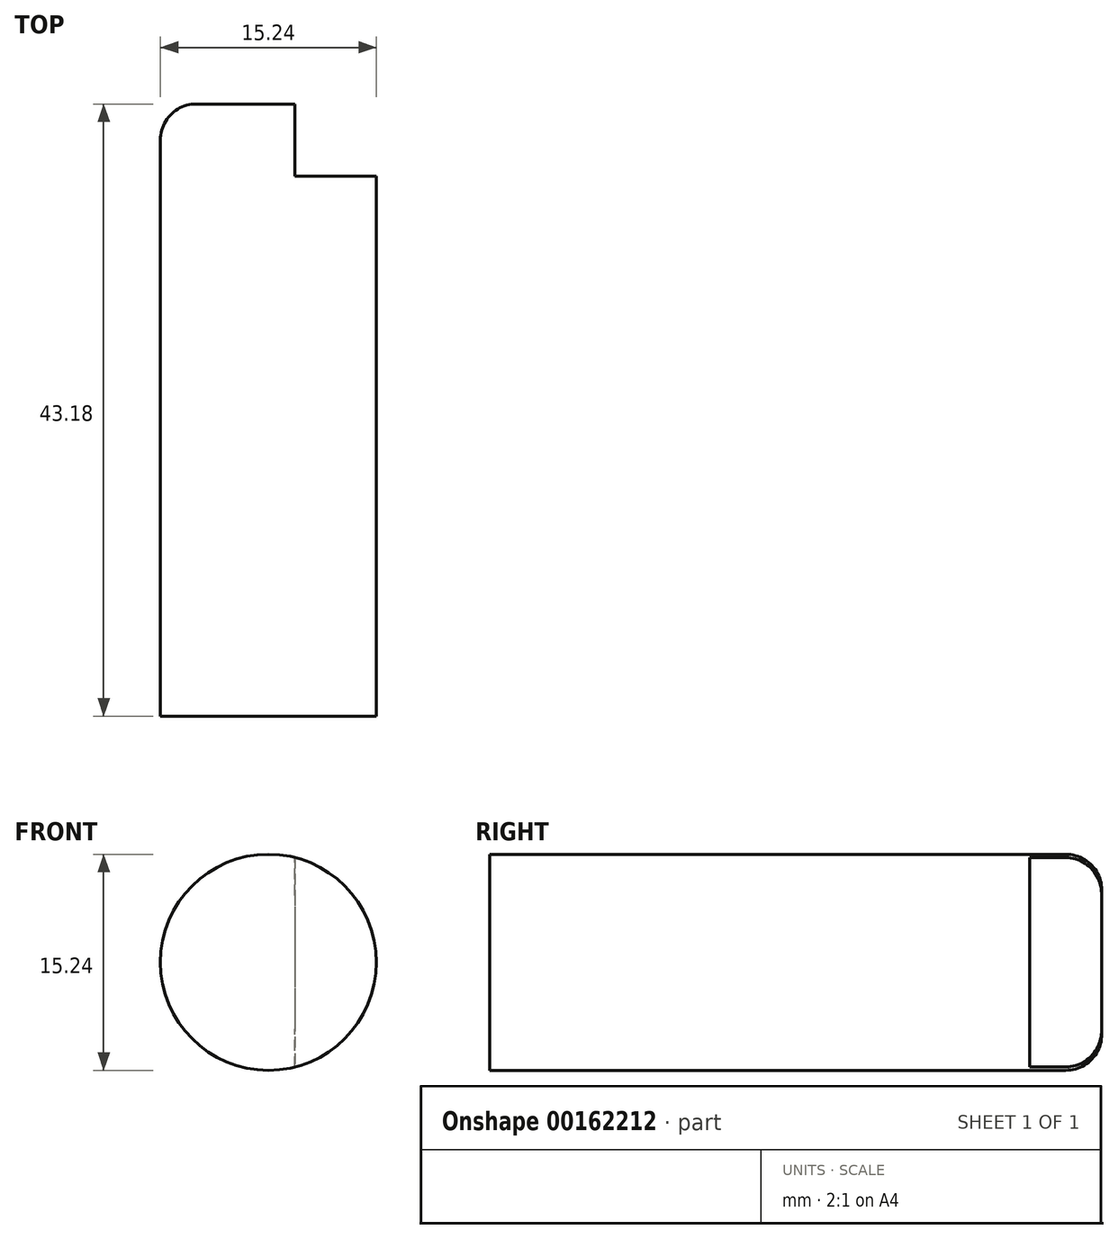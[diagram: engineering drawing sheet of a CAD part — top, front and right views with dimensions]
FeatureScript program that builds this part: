
annotation { "Feature Type Name" : "Feature", "Feature Type Description" : "" }
export const myFeature = defineFeature(function(context is Context, id is Id, definition is map)
    precondition{}
    {
        {
            var Q0;
            Q0=qCreatedBy(makeId("Front.planeOp"),FACE);
            var sketch = newSketch(context, id + "F0", { "sketchPlane" : qUnion([Q0])});
            skCircle(sketch, "E0", {"center": v(0, 0) * mm, "radius": 7.62 * mm});
            skSolve(sketch);
        }
        {
            var Q0;
            Q0 = qSketchRegion(id + "F0", true);
            extrude(context, id + "F1", {"entities" : qUnion([Q0]), "oppositeDirection" : true, "depth" : 43.18 * mm});
        }
        {
            var Q0;
            Q0=makeQuery(id+"F1.opExtrude","CAP_FACE",FACE,{"disambiguationData":[OSD([sQuery(id+"F0.wireOp",EDGE,"E0")])],"isStart":false});
            var sketch = newSketch(context, id + "F2", { "sketchPlane" : qUnion([Q0])});
            skArc(sketch, "E1.0", {"start": v(-1.86, 7.39) * mm, "mid": v(-7.62, 0) * mm, "end": v(-1.86, -7.39) * mm});
            skLineSegment(sketch, "E2", {"start": v(-1.86, 7.39) * mm, "end": v(-1.86, -7.39) * mm});
            skSolve(sketch);
        }
        {
            var Q0;
            Q0 = qSketchRegion(id + "F2", true);
            extrude(context, id + "F3", {"entities" : qUnion([Q0]), "operationType" : NewBodyOperationType.REMOVE, "oppositeDirection" : true, "depth" : 5.08 * mm});
        }
        {
            var Q0;
            Q0=makeQuery(id+"F1.opExtrude","CAP_EDGE",EDGE,{"disambiguationData":[OSD([sQuery(id+"F0.wireOp",EDGE,"E0")])],"isStart":false});
            fillet(context, id + "F4", {"entities" : qUnion([Q0]), "radius" : 2.54 * mm, "tangentPropagation" : true, "allowEdgeOverflow" : false});
        }
    });
